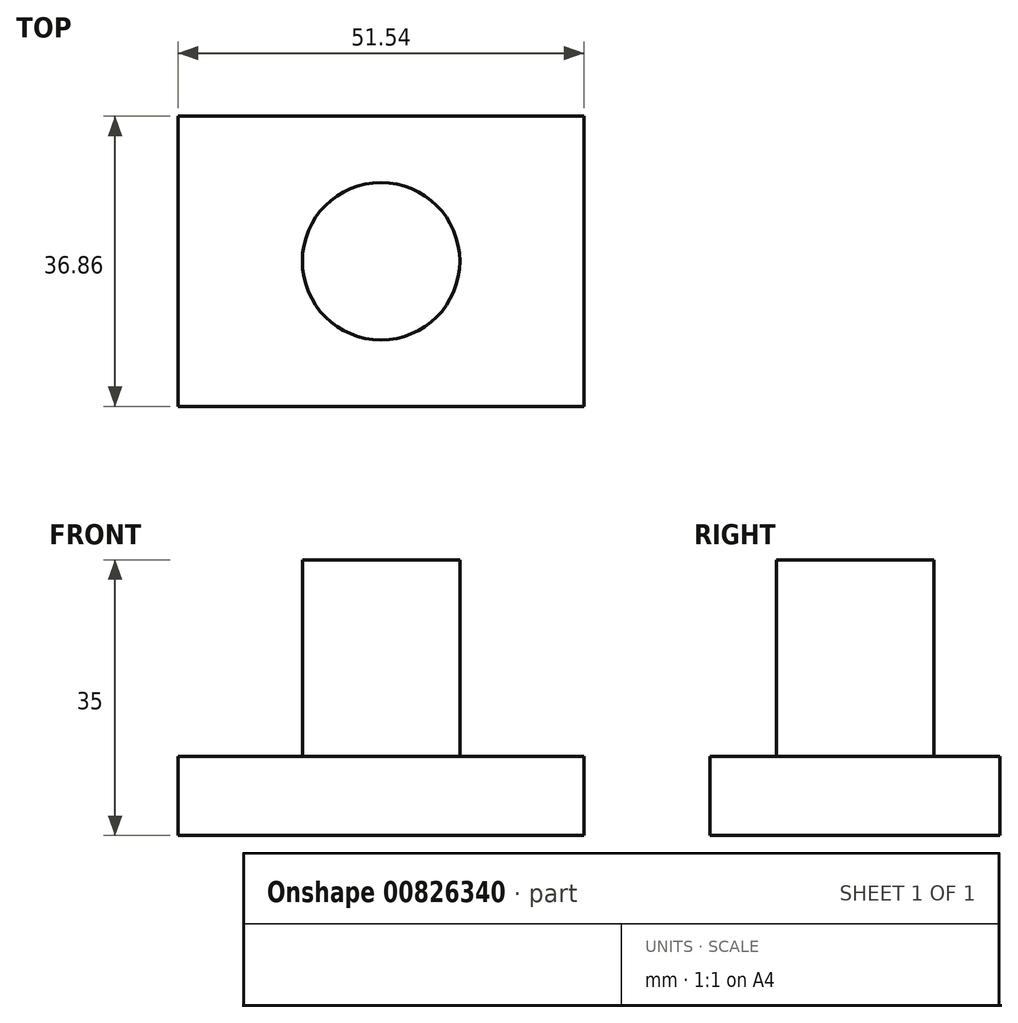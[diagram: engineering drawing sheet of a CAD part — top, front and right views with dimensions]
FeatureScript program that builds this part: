
annotation { "Feature Type Name" : "Feature", "Feature Type Description" : "" }
export const myFeature = defineFeature(function(context is Context, id is Id, definition is map)
    precondition{}
    {
        {
            var Q0;
            Q0=qCreatedBy(makeId("Top.planeOp"),FACE);
            var sketch = newSketch(context, id + "F0", { "sketchPlane" : qUnion([Q0])});
            skCircle(sketch, "E0", {"center": v(0, 0) * mm, "radius": 10 * mm});
            skSolve(sketch);
        }
        {
            var Q0;
            Q0=makeQuery(id+"F0.imprint","IMPRINT",FACE,{"disambiguationData":[TD([[makeQuery(id+"F0.imprint","IMPRINT",EDGE,{"derivedFrom":sQuery(id+"F0.wireOp",EDGE,"E0")}),1.0]])]});
            extrude(context, id + "F1", {"entities" : qUnion([Q0]), "depth" : 25 * mm, "offsetDistance" : 25 * mm});
        }
        {
            var Q0;
            Q0=qCreatedBy(makeId("Top.planeOp"),FACE);
            var sketch = newSketch(context, id + "F2", { "sketchPlane" : qUnion([Q0])});
            skLineSegment(sketch, "E1.bottom", {"start": v(-25.77, -18.43) * mm, "end": v(25.77, -18.43) * mm});
            skLineSegment(sketch, "E1.top", {"start": v(-25.77, 18.43) * mm, "end": v(25.77, 18.43) * mm});
            skLineSegment(sketch, "E1.left", {"start": v(-25.77, -18.43) * mm, "end": v(-25.77, 18.43) * mm});
            skLineSegment(sketch, "E1.right", {"start": v(25.77, -18.43) * mm, "end": v(25.77, 18.43) * mm});
            skPoint(sketch, "E1.middle", {"position": v(0, 0) * mm});
            skSolve(sketch);
        }
        {
            var Q0;
            Q0=makeQuery(id+"F2.imprint","IMPRINT",FACE,{"disambiguationData":[TD([[makeQuery(id+"F2.imprint","IMPRINT",EDGE,{"derivedFrom":sQuery(id+"F2.wireOp",EDGE,"E1.bottom")}),1.0]])]});
            extrude(context, id + "F3", {"entities" : qUnion([Q0]), "operationType" : NewBodyOperationType.ADD, "oppositeDirection" : true, "depth" : 10 * mm, "offsetDistance" : 25 * mm});
        }
    });
